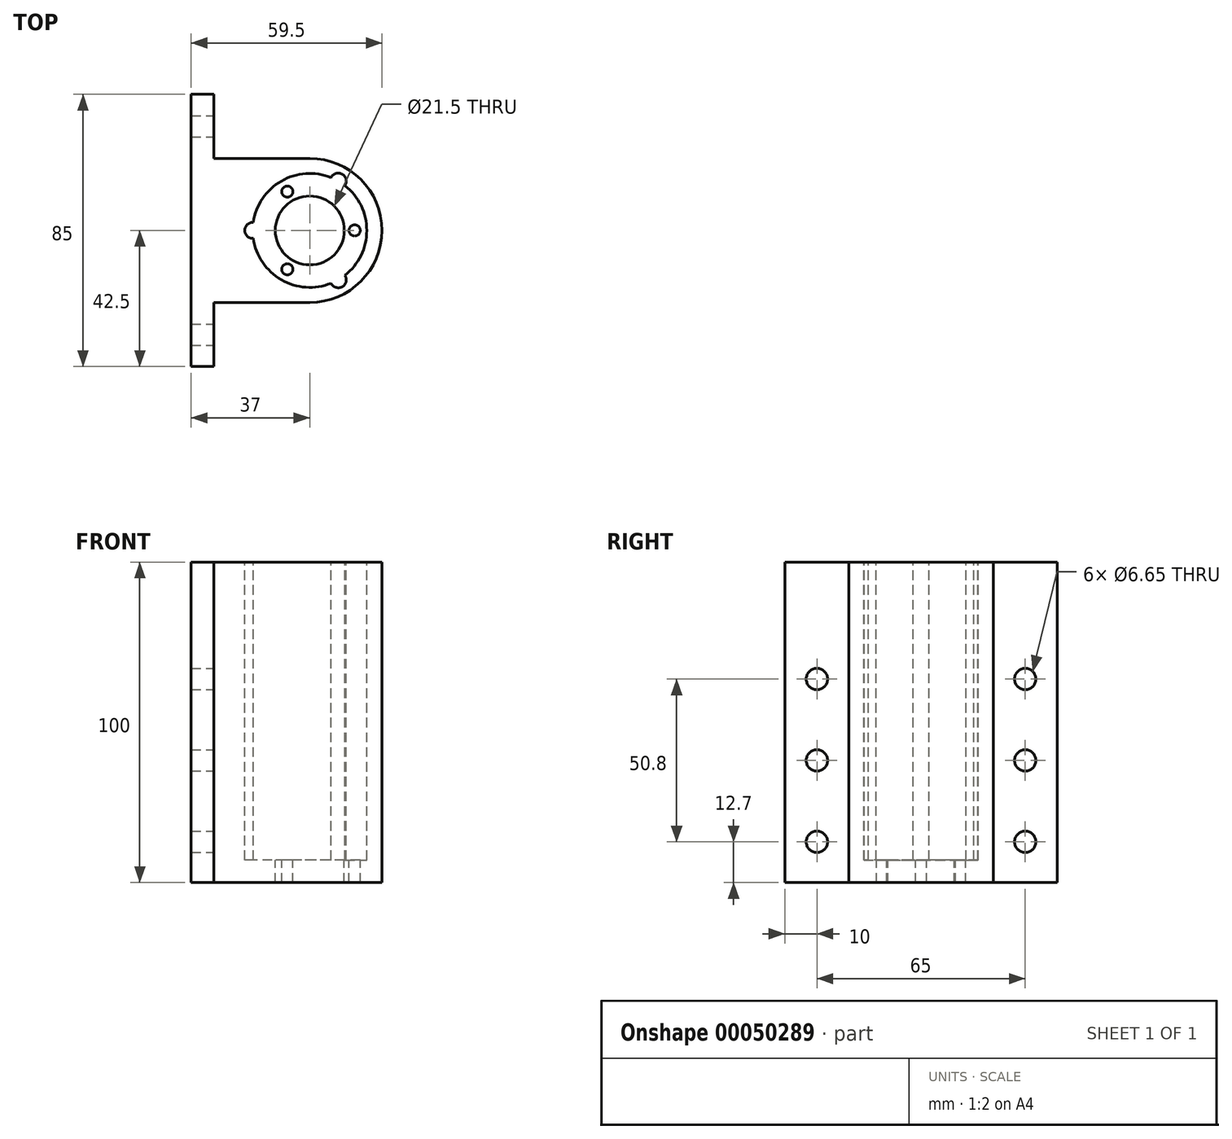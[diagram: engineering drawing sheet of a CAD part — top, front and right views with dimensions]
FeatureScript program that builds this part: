
annotation { "Feature Type Name" : "Feature", "Feature Type Description" : "" }
export const myFeature = defineFeature(function(context is Context, id is Id, definition is map)
    precondition{}
    {
        {
            var Q0;
            Q0=qCreatedBy(makeId("Top.planeOp"),FACE);
            var sketch = newSketch(context, id + "F0", { "sketchPlane" : qUnion([Q0])});
            skArc(sketch, "E0", {"start": v(0, -22.5) * mm, "mid": v(22.5, 0) * mm, "end": v(0, 22.5) * mm});
            skLineSegment(sketch, "E1.bottom", {"start": v(-30, -22.5) * mm, "end": v(0, -22.5) * mm});
            skLineSegment(sketch, "E1.top", {"start": v(-30, 22.5) * mm, "end": v(0, 22.5) * mm});
            skLineSegment(sketch, "E2.bottom", {"start": v(-37, -42.5) * mm, "end": v(-30, -42.5) * mm});
            skLineSegment(sketch, "E2.top", {"start": v(-37, 42.5) * mm, "end": v(-30, 42.5) * mm});
            skLineSegment(sketch, "E2.left", {"start": v(-37, -42.5) * mm, "end": v(-37, 42.5) * mm});
            skLineSegment(sketch, "E2.right", {"start": v(-30, -42.5) * mm, "end": v(-30, -22.5) * mm});
            skLineSegment(sketch, "E3.trimOffspring", {"start": v(-30, 22.5) * mm, "end": v(-30, 42.5) * mm});
            skSolve(sketch);
        }
        {
            var Q0;
            Q0=makeQuery(id+"F0.imprint","IMPRINT",FACE,{"disambiguationData":[TD([[makeQuery(id+"F0.imprint","IMPRINT",EDGE,{"derivedFrom":sQuery(id+"F0.wireOp",EDGE,"E0")}),1.0]])]});
            extrude(context, id + "F1", {"entities" : qUnion([Q0]), "depth" : 100 * mm});
        }
        {
            var Q0;
            Q0=makeQuery(id+"F1.opExtrude","CAP_FACE",FACE,{"disambiguationData":[OSD([sQuery(id+"F0.wireOp",EDGE,"E0")])],"isStart":false});
            var sketch = newSketch(context, id + "F2", { "sketchPlane" : qUnion([Q0])});
            skCircle(sketch, "E4", {"center": v(0, 0) * mm, "radius": 17.77 * mm});
            skCircle(sketch, "E5", {"center": v(-17.77, 0) * mm, "radius": 2.5 * mm});
            skCircle(sketch, "E6", {"center": v(8.89, -15.4) * mm, "radius": 2.5 * mm});
            skCircle(sketch, "E7", {"center": v(8.89, 15.4) * mm, "radius": 2.5 * mm});
            skSolve(sketch);
        }
        {
            var Q0;
            Q0 = qSketchRegion(id + "F2", true);
            extrude(context, id + "F3", {"entities" : qUnion([Q0]), "operationType" : NewBodyOperationType.REMOVE, "oppositeDirection" : true, "depth" : 93 * mm});
        }
        {
            var Q0;
            Q0=makeQuery(id+"F3.boolean.opBoolean","COPY",FACE,{"derivedFrom":makeQuery(id+"F3.opExtrude","CAP_FACE",FACE,{"disambiguationData":[OSD([sQuery(id+"F2.wireOp",EDGE,"E4")])],"isStart":false})});
            var sketch = newSketch(context, id + "F4", { "sketchPlane" : qUnion([Q0])});
            skCircle(sketch, "E8", {"center": v(0, 0) * mm, "radius": 10.75 * mm});
            skCircle(sketch, "E9", {"center": v(14, 0) * mm, "radius": 1.75 * mm});
            skCircle(sketch, "E10", {"center": v(-7, 12.13) * mm, "radius": 1.75 * mm});
            skCircle(sketch, "E11", {"center": v(-7, -12.13) * mm, "radius": 1.75 * mm});
            skSolve(sketch);
        }
        {
            var Q0;
            Q0 = qSketchRegion(id + "F4", true);
            extrude(context, id + "F5", {"entities" : qUnion([Q0]), "operationType" : NewBodyOperationType.REMOVE, "endBound" : BoundingType.THROUGH_ALL, "oppositeDirection" : true, "depth" : 25 * mm});
        }
        {
            var Q0;
            Q0=makeQuery(id+"F1.opExtrude","SWEPT_FACE",FACE,{"disambiguationData":[OSD([sQuery(id+"F0.wireOp",EDGE,"E3.trimOffspring")])]});
            var sketch = newSketch(context, id + "F6", { "sketchPlane" : qUnion([Q0])});
            skCircle(sketch, "E12", {"center": v(32.5, 12.7) * mm, "radius": 3.33 * mm});
            skCircle(sketch, "E13", {"center": v(-32.5, 12.7) * mm, "radius": 3.33 * mm});
            skCircle(sketch, "E14", {"center": v(-32.5, 63.5) * mm, "radius": 3.33 * mm});
            skCircle(sketch, "E15", {"center": v(32.5, 63.5) * mm, "radius": 3.33 * mm});
            skCircle(sketch, "E16", {"center": v(-32.5, 38.1) * mm, "radius": 3.33 * mm});
            skCircle(sketch, "E17", {"center": v(32.5, 38.1) * mm, "radius": 3.33 * mm});
            skSolve(sketch);
        }
        {
            var Q0;
            Q0 = qSketchRegion(id + "F6", true);
            extrude(context, id + "F7", {"entities" : qUnion([Q0]), "operationType" : NewBodyOperationType.REMOVE, "endBound" : BoundingType.THROUGH_ALL, "oppositeDirection" : true, "depth" : 25 * mm});
        }
    });
